# Revit family: Platek_Blend Applique 1 Opening
name_source: partatom
category: Apparecchi per illuminazione
revit_build: Autodesk Revit 2017 (Build: 20160225_1515(x64)
units: mm (PartAtom-declared; Revit-internal decimal feet)

## family parameters
Basato su piano di lavoro = No
Condiviso = No
Punto di calcolo locali = No
Quota connettore circolare = Usa diametro
Sempre verticale = Sì
Sorgente d'illuminazione = Sì
Taglio con vuoti quando caricato = No
Tipo di parte = Normale

## types (1)
- 1610117_10W_LED_3000K
    Angolo inclinazione = 90.00°
    Body = PLK_06_Grey
    CRI = >80
    Carico apparente = 0 VA
    Codice assieme = 1610117.02(White);  1610117.06(Grey);  1610117.01(Black);  1610117.08(Anthracite);  1610117.01(Black);  1610117.07(Corten);  1610117.09(Bronze)
    Colour Temperature = 3000 K
    Commenti sul tipo = Facades, Wall
    Descrizione = Outdoor Lighting, Wall mounted
    Diffuse Type = PMMA
    Dimmable = On request
    Emetti da larghezza rettangolo = 20 mm  [stored 0.0656168 ft]
    Emetti da lunghezza rettangolo = 130 mm  [stored 0.426509 ft]
    Energy Efficiency Rating = A/A+/A++
    File diagramma fotometrico = 1610117.IES
    Filtro dei colori = 16777215
    Frequency = 50/60 Hz
    IK Rating = IK05
    IP Rating = IP65
    Immagine tipo = blend_applique_1-2_finestre_1.jpg
    Insulation Class = 1
    LED Protection = Surge protection included
    Lampada = LED
    Light Source = PLK_Light Source
    Luminaire Luminous Flux = 700 lm
    Luminaire Luminous Intensity = 1069 cd
    Luminaire Wattage = 19 W
    Manufacturer Comment = 1 Opening
    Modello = Blend Applique 1Opening
    Mounting Type = Wall
    Nota chiave = Other LED colors available on request
    PLATEK Article Code = 1610117
    Part of body = PLK_Part of body
    Power Supply Unit = Included
    Product Dimension = L160mm x L160mm x 71,5mm
    Product Documentation Link = http://www.platek.eu
    Product Page URL = http://www.platek.eu
    Produttore = PLATEK SRL
    Rendi la forma visibile nel rendering = No
    Supply Voltage = 230 V
    Supply Voltage Max = 240 V
    Supply Voltage Min = 220 V
    URL = www.platek.eu
    Variazione temperatura colore lampada con luminosità attenuata = <Nessuno>

note: [stored X ft] marks values corroborated as IEEE doubles in the binary element streams (Revit-internal decimal feet)

## geometry (parser evidence)
native form markers: Blend x2
no freeform markers — native parametric forms only
